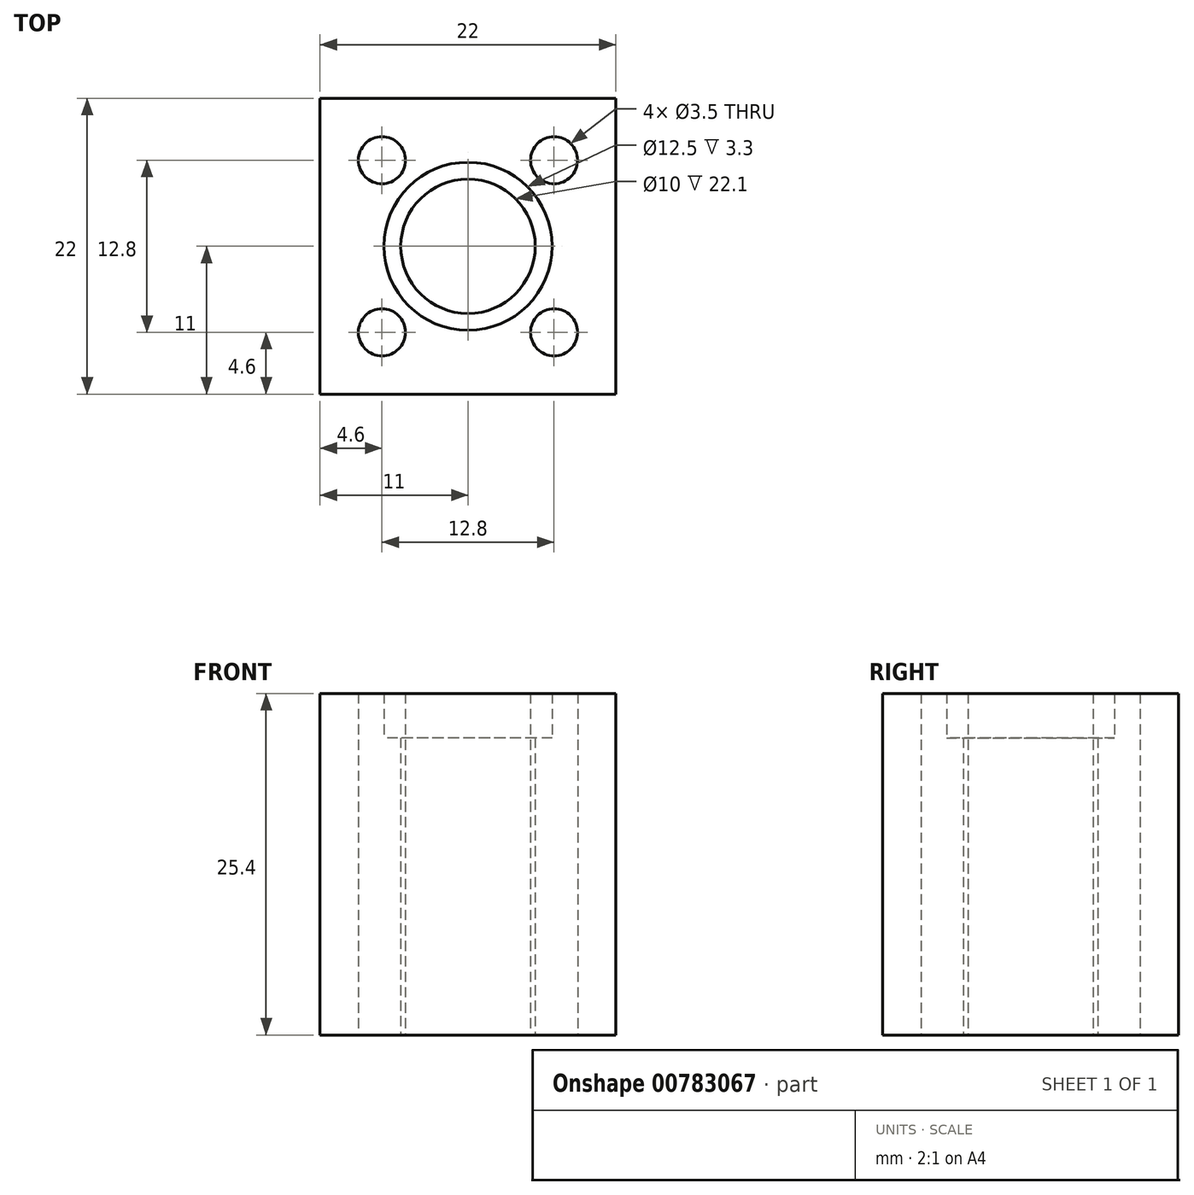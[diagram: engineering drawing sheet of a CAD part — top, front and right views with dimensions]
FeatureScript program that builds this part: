
annotation { "Feature Type Name" : "Feature", "Feature Type Description" : "" }
export const myFeature = defineFeature(function(context is Context, id is Id, definition is map)
    precondition{}
    {
        {
            var Q0;
            Q0=qCreatedBy(makeId("Top.planeOp"),FACE);
            var sketch = newSketch(context, id + "F0", { "sketchPlane" : qUnion([Q0])});
            skCircle(sketch, "E0", {"center": v(0, 0) * mm, "radius": 5 * mm});
            skLineSegment(sketch, "E1.bottom", {"start": v(11, -11) * mm, "end": v(-11, -11) * mm});
            skLineSegment(sketch, "E1.top", {"start": v(11, 11) * mm, "end": v(-11, 11) * mm});
            skLineSegment(sketch, "E1.left", {"start": v(11, -11) * mm, "end": v(11, 11) * mm});
            skLineSegment(sketch, "E1.right", {"start": v(-11, -11) * mm, "end": v(-11, 11) * mm});
            skCircle(sketch, "E2", {"center": v(0, 0) * mm, "radius": 6.25 * mm});
            skLineSegment(sketch, "E3.bottom", {"start": v(-11, 11) * mm, "end": v(-6.4, 11) * mm});
            skLineSegment(sketch, "E3.top", {"start": v(-11, 6.4) * mm, "end": v(-6.4, 6.4) * mm});
            skLineSegment(sketch, "E3.left", {"start": v(-11, 11) * mm, "end": v(-11, 6.4) * mm});
            skLineSegment(sketch, "E3.right", {"start": v(-6.4, 11) * mm, "end": v(-6.4, 6.4) * mm});
            skLineSegment(sketch, "E4.bottom", {"start": v(-11, -11) * mm, "end": v(-6.4, -11) * mm});
            skLineSegment(sketch, "E4.top", {"start": v(-11, -6.4) * mm, "end": v(-6.4, -6.4) * mm});
            skLineSegment(sketch, "E4.left", {"start": v(-11, -11) * mm, "end": v(-11, -6.4) * mm});
            skLineSegment(sketch, "E4.right", {"start": v(-6.4, -11) * mm, "end": v(-6.4, -6.4) * mm});
            skLineSegment(sketch, "E5.bottom", {"start": v(11, 11) * mm, "end": v(6.4, 11) * mm});
            skLineSegment(sketch, "E5.top", {"start": v(11, 6.4) * mm, "end": v(6.4, 6.4) * mm});
            skLineSegment(sketch, "E5.left", {"start": v(11, 11) * mm, "end": v(11, 6.4) * mm});
            skLineSegment(sketch, "E5.right", {"start": v(6.4, 11) * mm, "end": v(6.4, 6.4) * mm});
            skLineSegment(sketch, "E6.bottom", {"start": v(11, -11) * mm, "end": v(6.4, -11) * mm});
            skLineSegment(sketch, "E6.top", {"start": v(11, -6.4) * mm, "end": v(6.4, -6.4) * mm});
            skLineSegment(sketch, "E6.left", {"start": v(11, -11) * mm, "end": v(11, -6.4) * mm});
            skLineSegment(sketch, "E6.right", {"start": v(6.4, -11) * mm, "end": v(6.4, -6.4) * mm});
            skPoint(sketch, "E7", {"position": v(-6.4, 6.4) * mm});
            skPoint(sketch, "E8", {"position": v(6.4, 6.4) * mm});
            skPoint(sketch, "E9", {"position": v(6.4, -6.4) * mm});
            skPoint(sketch, "E10", {"position": v(-6.4, -6.4) * mm});
            skSolve(sketch);
        }
        {
            var Q0;
            Q0 = qSketchRegion(id + "F0", true);
            extrude(context, id + "F1", {"entities" : qUnion([Q0]), "depth" : 25.4 * mm, "offsetDistance" : 25 * mm});
        }
        {
            var Q0;
            Q0=makeQuery(id+"F0.imprint","IMPRINT",FACE,{"disambiguationData":[TD([[makeQuery(id+"F0.imprint","IMPRINT",EDGE,{"derivedFrom":sQuery(id+"F0.wireOp",EDGE,"E0")}),-1.0]])]});
            extrude(context, id + "F2", {"entities" : qUnion([Q0]), "operationType" : NewBodyOperationType.ADD, "depth" : 22.1 * mm, "offsetDistance" : 25 * mm});
        }
        {
            var Q0;
            Q0=sQuery(id+"F0.wireOp",VERTEX,"E10");
            var Q1;
            Q1=sQuery(id+"F0.wireOp",VERTEX,"E7");
            var Q2;
            Q2=sQuery(id+"F0.wireOp",VERTEX,"E9");
            var Q3;
            Q3=sQuery(id+"F0.wireOp",VERTEX,"E8");
            var Q4;
            Q4=makeQuery(id+"F1.opExtrude","SWEPT_BODY",BODY,{"disambiguationData":[OSD([sQuery(id+"F0.wireOp",EDGE,"E1.bottom"),sQuery(id+"F0.wireOp",EDGE,"E1.top"),sQuery(id+"F0.wireOp",EDGE,"E1.left"),sQuery(id+"F0.wireOp",EDGE,"E1.right"),sQuery(id+"F0.wireOp",EDGE,"E2"),sQuery(id+"F0.wireOp",EDGE,"E3.bottom"),sQuery(id+"F0.wireOp",EDGE,"E3.left"),sQuery(id+"F0.wireOp",EDGE,"E4.bottom"),sQuery(id+"F0.wireOp",EDGE,"E4.left"),sQuery(id+"F0.wireOp",EDGE,"E5.bottom"),sQuery(id+"F0.wireOp",EDGE,"E5.left"),sQuery(id+"F0.wireOp",EDGE,"E6.bottom"),sQuery(id+"F0.wireOp",EDGE,"E6.left")])]});
            hole(context, id + "F3", {"style" : HoleStyle.SIMPLE, "endStyle" : HoleEndStyle.THROUGH, "oppositeDirection" : true, "holeDiameter" : 3.5 * mm, "majorDiameter" : 5 * mm, "isTappedThrough" : true, "tappedDepth" : 12 * mm, "tapClearance" : 3, "locations" : qUnion([Q0, Q1, Q2, Q3]), "scope" : qUnion([Q4])});
        }
    });
